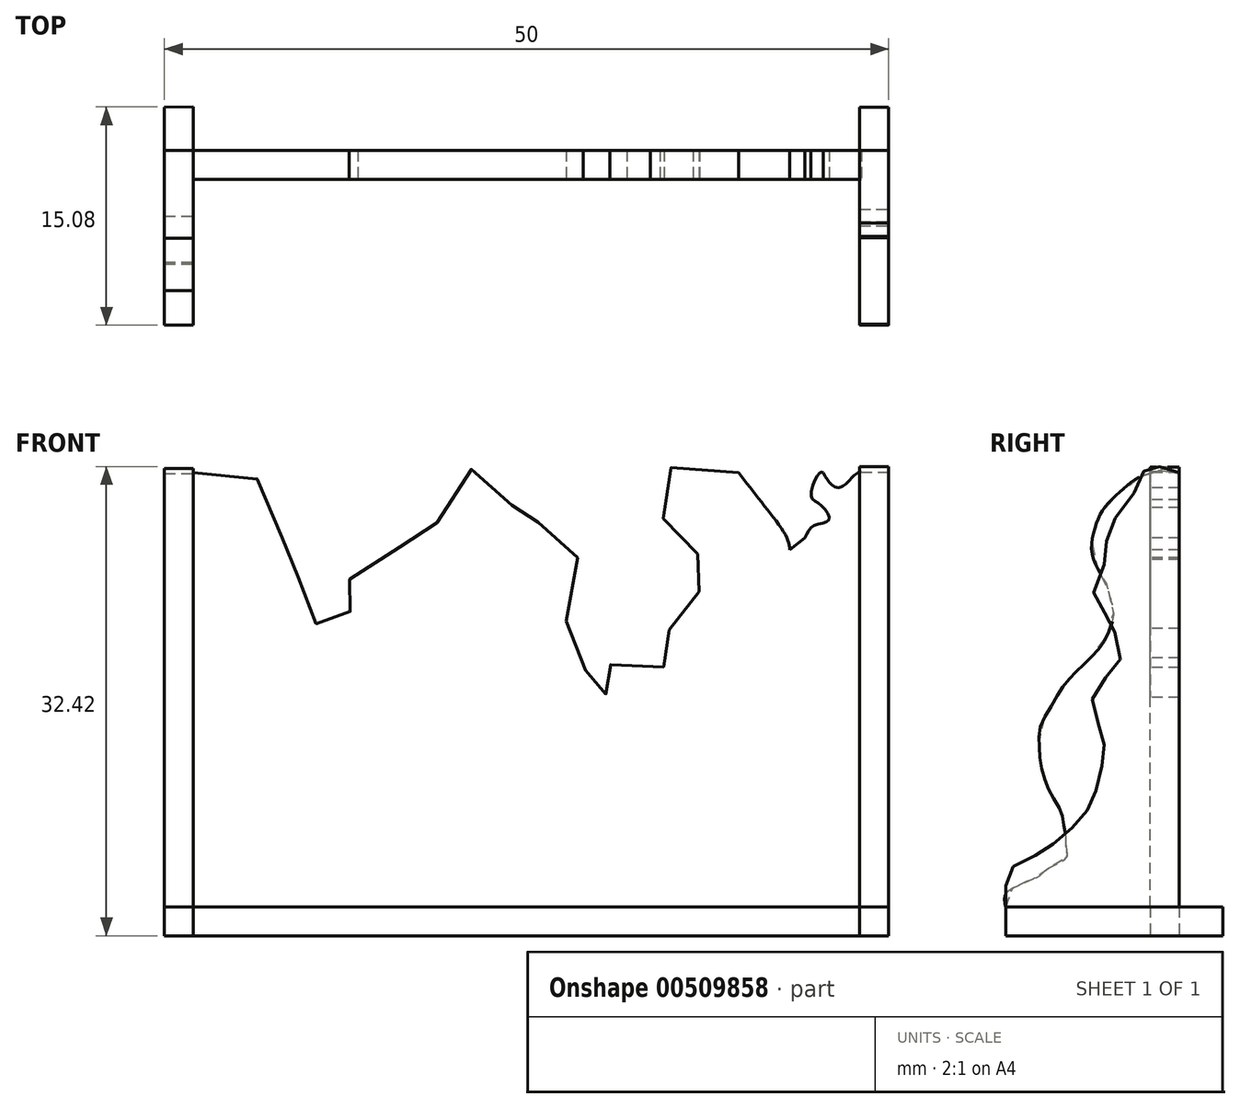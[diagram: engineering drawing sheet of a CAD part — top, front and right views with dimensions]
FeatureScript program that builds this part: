
annotation { "Feature Type Name" : "Feature", "Feature Type Description" : "" }
export const myFeature = defineFeature(function(context is Context, id is Id, definition is map)
    precondition{}
    {
        {
            var Q0;
            Q0=qCreatedBy(makeId("Top.planeOp"),FACE);
            var sketch = newSketch(context, id + "F0", { "sketchPlane" : qUnion([Q0])});
            skLineSegment(sketch, "E0", {"start": v(-34.37, 31.15) * mm, "end": v(15.63, 31.15) * mm});
            skLineSegment(sketch, "E1", {"start": v(-34.37, 31.15) * mm, "end": v(-34.37, 19.15) * mm});
            skLineSegment(sketch, "E2", {"start": v(15.63, 31.15) * mm, "end": v(15.63, 19.15) * mm});
            skLineSegment(sketch, "E3.0", {"start": v(-34.37, 29.15) * mm, "end": v(65.63, 29.15) * mm});
            skLineSegment(sketch, "E4.0", {"start": v(-32.37, 31.16) * mm, "end": v(-32.37, 19.15) * mm});
            skLineSegment(sketch, "E5", {"start": v(-34.37, 19.15) * mm, "end": v(-32.37, 19.15) * mm});
            skLineSegment(sketch, "E6.0", {"start": v(13.63, 31.15) * mm, "end": v(13.63, 19.15) * mm});
            skLineSegment(sketch, "E7", {"start": v(13.63, 19.15) * mm, "end": v(15.63, 19.15) * mm});
            skLineSegment(sketch, "E8", {"start": v(-34.37, 31.15) * mm, "end": v(-34.37, 34.15) * mm});
            skLineSegment(sketch, "E9", {"start": v(-32.37, 31.16) * mm, "end": v(-32.37, 34.16) * mm});
            skLineSegment(sketch, "E10", {"start": v(-32.37, 34.16) * mm, "end": v(-34.37, 34.15) * mm});
            skLineSegment(sketch, "E11", {"start": v(13.63, 31.15) * mm, "end": v(13.63, 34.15) * mm});
            skLineSegment(sketch, "E12", {"start": v(15.63, 31.15) * mm, "end": v(15.63, 34.15) * mm});
            skLineSegment(sketch, "E13", {"start": v(13.63, 34.15) * mm, "end": v(15.63, 34.15) * mm});
            skSolve(sketch);
        }
        {
            var Q0;
            Q0=qSketchRegion(id+"F0",true);
            extrude(context, id + "F1", {"entities" : qUnion([Q0]), "depth" : 2 * mm, "offsetDistance" : 25 * mm});
        }
        {
            var Q0;
            Q0=makeQuery(id+"F1.opExtrude","SWEPT_FACE",FACE,{"disambiguationData":[OSD([sQuery(id+"F0.wireOp",EDGE,"E3.0")])]});
            var sketch = newSketch(context, id + "F2", { "sketchPlane" : qUnion([Q0])});
            skLineSegment(sketch, "E14", {"start": v(-32.37, 2) * mm, "end": v(-32.37, 32) * mm});
            skLineSegment(sketch, "E15", {"start": v(13.63, 2) * mm, "end": v(13.63, 32) * mm});
            skLineSegment(sketch, "E16", {"start": v(-32.37, 2) * mm, "end": v(13.63, 2) * mm});
            skFitSpline(sketch, "E17", {"points": [v(-32.37, 32) * mm, v(-28.3, 32) * mm, v(-27.26, 29.16) * mm, v(-25.6, 26.66) * mm, v(-25.18, 25.62) * mm, v(-24.97, 23.53) * mm, v(-23.93, 21.65) * mm, v(-23.72, 21.24) * mm, v(-22.47, 21.86) * mm, v(-21, 22.9) * mm, v(-21.42, 23.53) * mm, v(-21.22, 25.4) * mm, v(-18.09, 26.87) * mm, v(-16.42, 27.91) * mm, v(-15.38, 28.74) * mm, v(-13.5, 32) * mm, v(-12.04, 32) * mm, v(-9.96, 29.58) * mm, v(-8.74, 30.1) * mm, v(-8.08, 26.24) * mm, v(-5.58, 26.01) * mm, v(-6.62, 21.86) * mm, v(-5.79, 19.36) * mm, v(-5.16, 17.9) * mm, v(-4.95, 17.28) * mm, v(-4.33, 16.86) * mm, v(-2.45, 16.65) * mm, v(-3.58, 19.1) * mm, v(0, 18.53) * mm, v(0, 19.15) * mm, v(0, 20.61) * mm, v(1.72, 22.07) * mm, v(2.56, 23.74) * mm, v(2.14, 24.16) * mm, v(2.56, 26.03) * mm, v(1.51, 27.08) * mm, v(0, 28.95) * mm, v(-0.48, 32) * mm, v(4.85, 32) * mm, v(5.27, 32) * mm], "startDerivative": vector(129.7, 24.67) * mm, "endDerivative": vector(25.98, 3.35) * mm});
            skFitSpline(sketch, "E18", {"points": [v(5.27, 32) * mm, v(7.14, 29.58) * mm, v(8.6, 27.5) * mm, v(8.81, 26.66) * mm], "startDerivative": vector(4.5, -5.85) * mm, "endDerivative": vector(0.4, -3.51) * mm});
            skFitSpline(sketch, "E19", {"points": [v(9.85, 27.5) * mm, v(10.48, 28.33) * mm, v(11.52, 28.74) * mm, v(10.9, 29.79) * mm, v(10.27, 30.41) * mm, v(10.9, 32) * mm, v(11.1, 32) * mm], "startDerivative": vector(2.44, 5.75) * mm, "endDerivative": vector(2.4, -1.22) * mm});
            skFitSpline(sketch, "E20", {"points": [v(13.82, 32.08) * mm, v(13.63, 32) * mm], "startDerivative": vector(-0.19, -0.08) * mm, "endDerivative": vector(-0.19, -0.08) * mm});
            skFitSpline(sketch, "E21", {"points": [v(8.81, 26.66) * mm, v(9.85, 27.5) * mm], "startDerivative": vector(1.04, 0.83) * mm, "endDerivative": vector(1.04, 0.83) * mm});
            skFitSpline(sketch, "E22", {"points": [v(11.1, 32) * mm, v(13.75, 32.05) * mm], "startDerivative": vector(3.79, -7.12) * mm, "endDerivative": vector(2.65, 0.05) * mm});
            skSolve(sketch);
        }
        {
            var Q0;
            Q0=qSketchRegion(id+"F2",true);
            extrude(context, id + "F3", {"entities" : qUnion([Q0]), "oppositeDirection" : true, "depth" : 2 * mm, "offsetDistance" : 25 * mm});
        }
        {
            var Q0;
            Q0=makeQuery(id+"F1.opExtrude","SWEPT_FACE",FACE,{"disambiguationData":[OSD([sQuery(id+"F0.wireOp",EDGE,"E4.0")])]});
            var sketch = newSketch(context, id + "F4", { "sketchPlane" : qUnion([Q0])});
            skLineSegment(sketch, "E23", {"start": v(19.15, 2) * mm, "end": v(31.15, 2) * mm});
            skLineSegment(sketch, "E24", {"start": v(31.15, 2) * mm, "end": v(31.15, 31.94) * mm});
            skFitSpline(sketch, "E25", {"points": [v(19.15, 2) * mm, v(19.15, 2.87) * mm, v(19.96, 3.46) * mm, v(20.88, 3.88) * mm, v(21.47, 4.13) * mm, v(22.06, 4.64) * mm, v(22.74, 4.97) * mm, v(23.41, 5.48) * mm, v(23.33, 6.15) * mm, v(23.33, 6.83) * mm, v(23.16, 7.75) * mm, v(23, 8.6) * mm, v(22.4, 9.6) * mm, v(21.9, 10.7) * mm, v(21.56, 12.05) * mm, v(21.47, 13.31) * mm, v(21.56, 14.4) * mm, v(22.23, 15.75) * mm, v(23, 17.02) * mm, v(23.66, 17.86) * mm, v(24.5, 18.7) * mm, v(25.43, 19.63) * mm, v(26.02, 20.47) * mm, v(26.53, 21.65) * mm, v(26.61, 22.4) * mm, v(26.36, 23.5) * mm, v(26.1, 24.34) * mm, v(25.6, 25.19) * mm, v(25.1, 26.62) * mm, v(25.35, 28.22) * mm, v(25.85, 29.4) * mm, v(26.86, 30.5) * mm, v(27.96, 31.42) * mm, v(28.97, 31.92) * mm, v(29.56, 32.1) * mm, v(30.4, 32.26) * mm, v(31.15, 31.94) * mm], "startDerivative": vector(-7.3, 37.36) * mm, "endDerivative": vector(29.43, -18.38) * mm});
            skSolve(sketch);
        }
        {
            var Q0;
            Q0=qSketchRegion(id+"F4",true);
            extrude(context, id + "F5", {"entities" : qUnion([Q0]), "oppositeDirection" : true, "depth" : 2 * mm, "offsetDistance" : 25 * mm});
        }
        {
            var Q0;
            Q0=makeQuery(id+"F1.opExtrude","SWEPT_FACE",FACE,{"disambiguationData":[OSD([sQuery(id+"F0.wireOp",EDGE,"E6.0")])]});
            var sketch = newSketch(context, id + "F6", { "sketchPlane" : qUnion([Q0])});
            skLineSegment(sketch, "E26", {"start": v(-19.15, 2) * mm, "end": v(-31.15, 2) * mm});
            skLineSegment(sketch, "E27", {"start": v(-31.15, 2) * mm, "end": v(-31.15, 32) * mm});
            skFitSpline(sketch, "E28", {"points": [v(-19.15, 2) * mm, v(-19.15, 2.85) * mm, v(-19.15, 3.55) * mm, v(-19.15, 4.25) * mm, v(-20.13, 5.05) * mm, v(-21.03, 5.45) * mm, v(-21.53, 5.75) * mm, v(-22.33, 6.25) * mm, v(-23.04, 6.76) * mm, v(-23.94, 7.66) * mm, v(-24.54, 8.26) * mm, v(-25.04, 9.06) * mm, v(-25.34, 9.76) * mm, v(-25.54, 10.76) * mm, v(-25.84, 11.86) * mm, v(-25.94, 12.56) * mm, v(-25.94, 13.47) * mm, v(-25.74, 14.27) * mm, v(-25.34, 15.17) * mm, v(-25.14, 16.27) * mm, v(-25.54, 17.27) * mm, v(-26.44, 18.17) * mm, v(-27.04, 18.87) * mm, v(-26.94, 20.08) * mm, v(-26.64, 21.28) * mm, v(-26.44, 21.88) * mm, v(-25.44, 22.88) * mm, v(-25.24, 23.58) * mm, v(-25.54, 24.78) * mm, v(-26.24, 26.39) * mm, v(-26.14, 27.09) * mm, v(-26.34, 28.29) * mm, v(-26.94, 29.09) * mm, v(-28.04, 30.6) * mm, v(-28.34, 31.6) * mm, v(-28.84, 32.2) * mm, v(-29.14, 32.3) * mm, v(-29.75, 32.4) * mm, v(-30.25, 32.4) * mm, v(-31.15, 32) * mm], "startDerivative": vector(0.55, 35.94) * mm, "endDerivative": vector(-37.5, -19.29) * mm});
            skSolve(sketch);
        }
        {
            var Q0;
            Q0=qSketchRegion(id+"F6",true);
            extrude(context, id + "F7", {"entities" : qUnion([Q0]), "oppositeDirection" : true, "depth" : 2 * mm, "offsetDistance" : 25 * mm});
        }
    });
